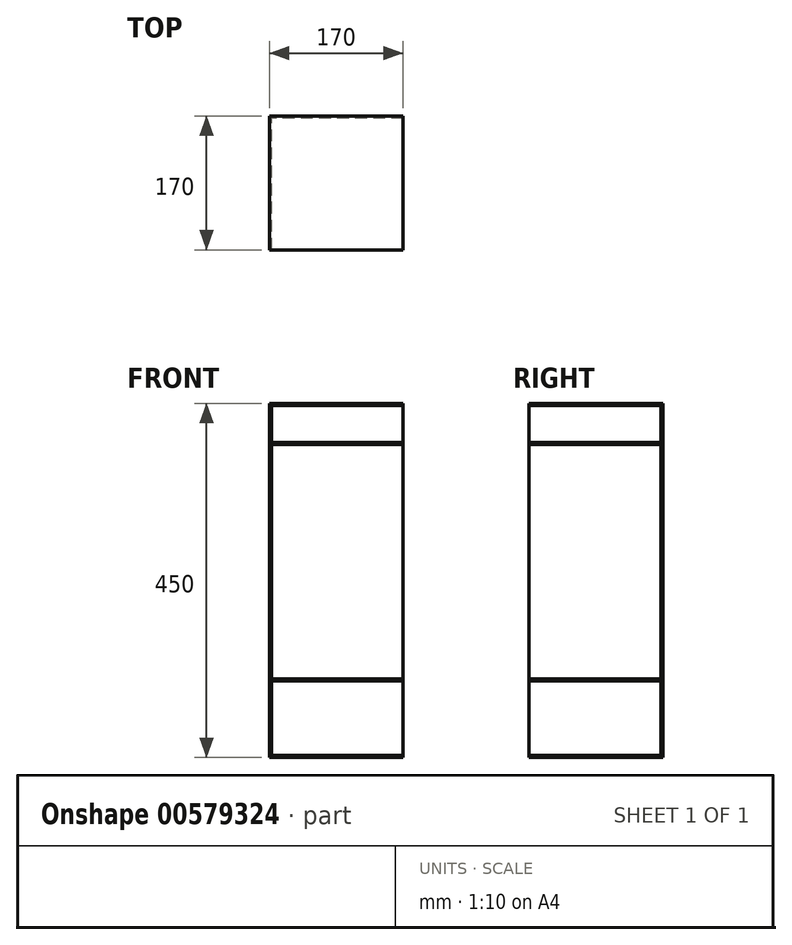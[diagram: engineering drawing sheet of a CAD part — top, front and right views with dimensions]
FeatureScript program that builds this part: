
annotation { "Feature Type Name" : "Feature", "Feature Type Description" : "" }
export const myFeature = defineFeature(function(context is Context, id is Id, definition is map)
    precondition{}
    {
        {
            var Q0;
            Q0=qCreatedBy(makeId("Top.planeOp"),FACE);
            var sketch = newSketch(context, id + "F0", { "sketchPlane" : qUnion([Q0])});
            skLineSegment(sketch, "E0.bottom", {"start": v(85, -85) * mm, "end": v(-85, -85) * mm});
            skLineSegment(sketch, "E0.top", {"start": v(85, 85) * mm, "end": v(-85, 85) * mm});
            skLineSegment(sketch, "E0.left", {"start": v(85, -85) * mm, "end": v(85, 85) * mm});
            skLineSegment(sketch, "E0.right", {"start": v(-85, -85) * mm, "end": v(-85, 85) * mm});
            skPoint(sketch, "E0.middle", {"position": v(0, 0) * mm});
            skLineSegment(sketch, "E1", {"start": v(-85, 85) * mm, "end": v(-85, 82.5) * mm});
            skLineSegment(sketch, "E2", {"start": v(-85, 82.5) * mm, "end": v(85, 82.5) * mm});
            skLineSegment(sketch, "E3", {"start": v(85, -85) * mm, "end": v(82.5, -85) * mm});
            skLineSegment(sketch, "E4", {"start": v(82.5, -85) * mm, "end": v(82.5, 85) * mm});
            skLineSegment(sketch, "E5.bottom", {"start": v(-85, 82.5) * mm, "end": v(82.5, 82.5) * mm});
            skLineSegment(sketch, "E5.top", {"start": v(-85, 0) * mm, "end": v(82.5, 0) * mm});
            skLineSegment(sketch, "E5.left", {"start": v(-85, 82.5) * mm, "end": v(-85, 0) * mm});
            skLineSegment(sketch, "E5.right", {"start": v(82.5, 82.5) * mm, "end": v(82.5, 0) * mm});
            skSolve(sketch);
        }
        {
            var Q0;
            Q0 = qSketchRegion(id + "F0", true);
            extrude(context, id + "F1", {"entities" : qUnion([Q0]), "depth" : 100 * mm, "offsetDistance" : 25 * mm});
        }
        {
            var Q0;
            Q0=makeQuery(id+"F1.opExtrude","SWEPT_FACE",FACE,{"disambiguationData":[OSD([sQuery(id+"F0.wireOp",EDGE,"E0.left")])]});
            var Q1;
            Q1=makeQuery(id+"F1.opExtrude","SWEPT_FACE",FACE,{"disambiguationData":[OSD([sQuery(id+"F0.wireOp",EDGE,"E0.bottom"),sQuery(id+"F0.wireOp",EDGE,"E3")])]});
            shell(context, id + "F2", {"entities" : qUnion([Q0, Q1]), "thickness" : 2.5 * mm});
        }
        {
            var Q0;
            Q0=makeQuery(id+"F1.opExtrude","CAP_FACE",FACE,{"disambiguationData":[OSD([sQuery(id+"F0.wireOp",EDGE,"E0.bottom"),sQuery(id+"F0.wireOp",EDGE,"E0.top"),sQuery(id+"F0.wireOp",EDGE,"E0.left"),sQuery(id+"F0.wireOp",EDGE,"E0.right"),sQuery(id+"F0.wireOp",EDGE,"E1"),sQuery(id+"F0.wireOp",EDGE,"E3"),sQuery(id+"F0.wireOp",EDGE,"E5.left")])],"isStart":false});
            var sketch = newSketch(context, id + "F3", { "sketchPlane" : qUnion([Q0])});
            skLineSegment(sketch, "E6.bottom", {"start": v(-85, -85) * mm, "end": v(85, -85) * mm});
            skLineSegment(sketch, "E6.top", {"start": v(-85, 85) * mm, "end": v(85, 85) * mm});
            skLineSegment(sketch, "E6.left", {"start": v(-85, -85) * mm, "end": v(-85, 85) * mm});
            skLineSegment(sketch, "E6.right", {"start": v(85, -85) * mm, "end": v(85, 85) * mm});
            skPoint(sketch, "E6.middle", {"position": v(0, 0) * mm});
            skLineSegment(sketch, "E7", {"start": v(-85, -85) * mm, "end": v(-82.5, -85) * mm});
            skLineSegment(sketch, "E8", {"start": v(-82.5, -85) * mm, "end": v(-82.5, 85) * mm});
            skLineSegment(sketch, "E9", {"start": v(-82.5, 85) * mm, "end": v(85, 85) * mm});
            skLineSegment(sketch, "E10", {"start": v(85, 82.5) * mm, "end": v(-85, 82.5) * mm});
            skSolve(sketch);
        }
        {
            var Q0;
            Q0 = qSketchRegion(id + "F3", true);
            extrude(context, id + "F4", {"entities" : qUnion([Q0]), "operationType" : NewBodyOperationType.ADD, "depth" : 300 * mm, "offsetDistance" : 25 * mm});
        }
        {
            var Q0;
            Q0=makeQuery(id+"F4.boolean.opBoolean","MERGE",FACE,{"derivedFrom":[makeQuery(id+"F1.opExtrude","SWEPT_FACE",FACE,{"disambiguationData":[OSD([sQuery(id+"F0.wireOp",EDGE,"E0.left")])]}),makeQuery(id+"F4.opExtrude","SWEPT_FACE",FACE,{"disambiguationData":[OSD([sQuery(id+"F3.wireOp",EDGE,"E6.right")])]})]});
            var Q1;
            Q1=makeQuery(id+"F4.boolean.opBoolean","MERGE",FACE,{"derivedFrom":[makeQuery(id+"F1.opExtrude","SWEPT_FACE",FACE,{"disambiguationData":[OSD([sQuery(id+"F0.wireOp",EDGE,"E0.bottom"),sQuery(id+"F0.wireOp",EDGE,"E3")])]}),makeQuery(id+"F4.opExtrude","SWEPT_FACE",FACE,{"disambiguationData":[OSD([sQuery(id+"F3.wireOp",EDGE,"E6.bottom"),sQuery(id+"F3.wireOp",EDGE,"E7")])]})]});
            shell(context, id + "F5", {"entities" : qUnion([Q0, Q1]), "thickness" : 2.5 * mm});
        }
        {
            var Q0;
            Q0=makeQuery(id+"F4.opExtrude","CAP_FACE",FACE,{"disambiguationData":[OSD([sQuery(id+"F3.wireOp",EDGE,"E6.bottom"),sQuery(id+"F3.wireOp",EDGE,"E6.top"),sQuery(id+"F3.wireOp",EDGE,"E6.left"),sQuery(id+"F3.wireOp",EDGE,"E6.right"),sQuery(id+"F3.wireOp",EDGE,"E7"),sQuery(id+"F3.wireOp",EDGE,"E9")])],"isStart":false});
            extrude(context, id + "F6", {"entities" : qUnion([Q0]), "operationType" : NewBodyOperationType.ADD, "depth" : 50 * mm, "offsetDistance" : 25 * mm});
        }
        {
            var Q0;
            {var subQ0=sQuery(id+"F3.wireOp",EDGE,"E7");var subQ1=sQuery(id+"F3.wireOp",EDGE,"E6.bottom");Q0=makeQuery(id+"F6.boolean.opBoolean","MERGE",FACE,{"derivedFrom":[makeQuery(id+"F4.boolean.opBoolean","MERGE",FACE,{"derivedFrom":[makeQuery(id+"F1.opExtrude","SWEPT_FACE",FACE,{"disambiguationData":[OSD([sQuery(id+"F0.wireOp",EDGE,"E0.bottom"),sQuery(id+"F0.wireOp",EDGE,"E3")])]}),makeQuery(id+"F4.opExtrude","SWEPT_FACE",FACE,{"disambiguationData":[OSD([subQ1,subQ0])]})]}),makeQuery(id+"F6.opExtrude","SWEPT_FACE",FACE,{"disambiguationData":[OSD([subQ1,subQ0])]})]});}
            var Q1;
            {var subQ0=sQuery(id+"F3.wireOp",EDGE,"E6.right");Q1=makeQuery(id+"F6.boolean.opBoolean","MERGE",FACE,{"derivedFrom":[makeQuery(id+"F4.boolean.opBoolean","MERGE",FACE,{"derivedFrom":[makeQuery(id+"F1.opExtrude","SWEPT_FACE",FACE,{"disambiguationData":[OSD([sQuery(id+"F0.wireOp",EDGE,"E0.left")])]}),makeQuery(id+"F4.opExtrude","SWEPT_FACE",FACE,{"disambiguationData":[OSD([subQ0])]})]}),makeQuery(id+"F6.opExtrude","SWEPT_FACE",FACE,{"disambiguationData":[OSD([subQ0])]})]});}
            shell(context, id + "F7", {"entities" : qUnion([Q0, Q1]), "thickness" : 2.5 * mm});
        }
    });
